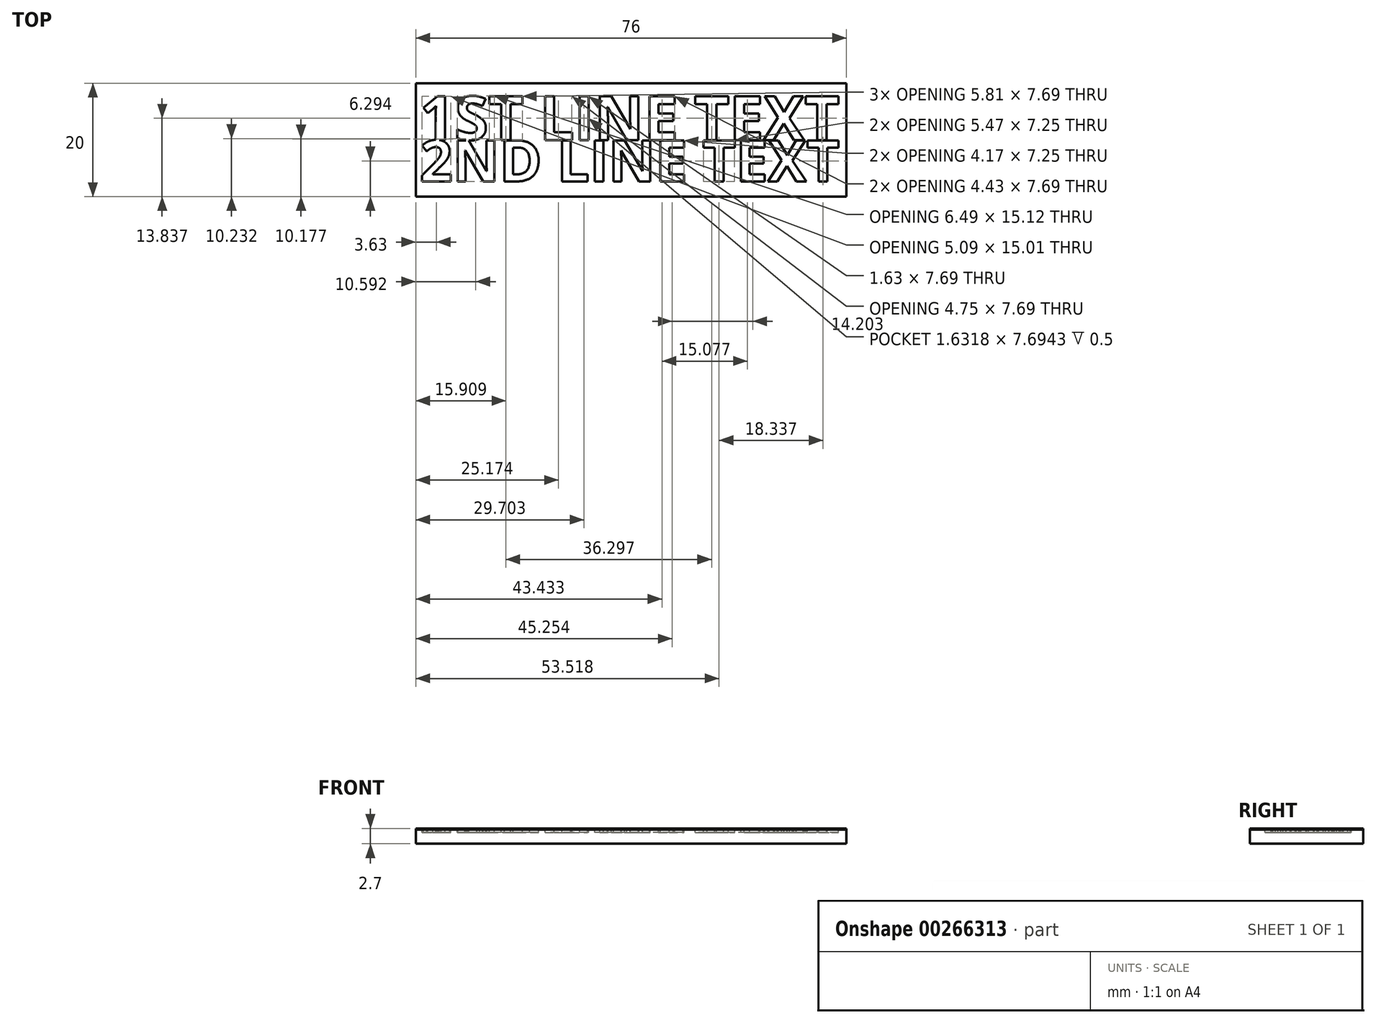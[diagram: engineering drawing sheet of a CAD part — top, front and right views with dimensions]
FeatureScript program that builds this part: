
annotation { "Feature Type Name" : "Feature", "Feature Type Description" : "" }
export const myFeature = defineFeature(function(context is Context, id is Id, definition is map)
    precondition{}
    {
        {
            var Q0;
            Q0=qCreatedBy(makeId("Top.planeOp"),FACE);
            var sketch = newSketch(context, id + "F0", { "sketchPlane" : qUnion([Q0])});
            skLineSegment(sketch, "E0.bottom", {"start": v(38, -10) * mm, "end": v(-38, -10) * mm});
            skLineSegment(sketch, "E0.top", {"start": v(38, 10) * mm, "end": v(-38, 10) * mm});
            skLineSegment(sketch, "E0.left", {"start": v(38, -10) * mm, "end": v(38, 10) * mm});
            skLineSegment(sketch, "E0.right", {"start": v(-38, -10) * mm, "end": v(-38, 10) * mm});
            skPoint(sketch, "E0.middle", {"position": v(0, 0) * mm});
            skSolve(sketch);
        }
        {
            var Q0;
            Q0=makeQuery(id+"F0.imprint","IMPRINT",FACE,{"disambiguationData":[TD([[makeQuery(id+"F0.imprint","IMPRINT",EDGE,{"derivedFrom":sQuery(id+"F0.wireOp",EDGE,"E0.bottom")}),-1.0]])]});
            extrude(context, id + "F1", {"entities" : qUnion([Q0]), "depth" : 2.5 * mm});
        }
        {
            var Q0;
            Q0=makeQuery(id+"F1.opExtrude","CAP_FACE",FACE,{"disambiguationData":[OSD([sQuery(id+"F0.wireOp",EDGE,"E0.bottom"),sQuery(id+"F0.wireOp",EDGE,"E0.top"),sQuery(id+"F0.wireOp",EDGE,"E0.left"),sQuery(id+"F0.wireOp",EDGE,"E0.right")])],"isStart":false});
            var sketch = newSketch(context, id + "F2", { "sketchPlane" : qUnion([Q0])});
            skText(sketch, "E1", { "text": "1ST LINE TEXT", "fontName": "OpenSans-Bold.ttf"});
            skText(sketch, "E2", { "text": "2ND LINE TEXT", "fontName": "OpenSans-Bold.ttf"});
            const initialGuessF2  = {"E1": [-0.0373, -1e-05, 1, 0, 0.00776], "E2": [-0.0373, -0.00733, 1, 0, 0.00731]};
            skSetInitialGuess(sketch, initialGuessF2);
            skSolve(sketch);
        }
        {
            var Q0;
            Q0=qSketchRegion(id+"F2",true);
            extrude(context, id + "F3", {"entities" : qUnion([Q0]), "operationType" : NewBodyOperationType.REMOVE, "oppositeDirection" : true, "depth" : 0.5 * mm});
        }
        {
            var Q0;
            {var subQ0=sQuery(id+"F0.wireOp",EDGE,"E0.bottom");var subQ1=sQuery(id+"F0.wireOp",EDGE,"E0.right");var subQ2=sQuery(id+"F0.wireOp",EDGE,"E0.left");var subQ3=sQuery(id+"F0.wireOp",EDGE,"E0.top");Q0=makeQuery(id+"F3.boolean.opBoolean","SPLIT",FACE,{"disambiguationData":[TD([makeQuery(id+"F1.opExtrude","SWEPT_FACE",FACE,{"disambiguationData":[OSD([subQ0])]})])],"derivedFrom":makeQuery(id+"F1.opExtrude","CAP_FACE",FACE,{"disambiguationData":[OSD([subQ0,subQ3,subQ2,subQ1])],"isStart":false})});}
            var Q1;
            Q1=makeQuery(id+"F3.boolean.opBoolean","SPLIT",FACE,{"disambiguationData":[TD([makeQuery(id+"F3.opExtrude","SWEPT_FACE",FACE,{"disambiguationData":[OSD([sQuery(id+"F2.wireOp",EDGE,"E1.sketch_text.stroke-8")])]})])],"derivedFrom":makeQuery(id+"F1.opExtrude","CAP_FACE",FACE,{"disambiguationData":[OSD([sQuery(id+"F0.wireOp",EDGE,"E0.bottom"),sQuery(id+"F0.wireOp",EDGE,"E0.top"),sQuery(id+"F0.wireOp",EDGE,"E0.left"),sQuery(id+"F0.wireOp",EDGE,"E0.right")])],"isStart":false})});
            var Q2;
            Q2=makeQuery(id+"F3.boolean.opBoolean","SPLIT",FACE,{"disambiguationData":[TD([makeQuery(id+"F3.opExtrude","SWEPT_FACE",FACE,{"disambiguationData":[OSD([sQuery(id+"F2.wireOp",EDGE,"E2.sketch_text.stroke-45")])]})])],"derivedFrom":makeQuery(id+"F1.opExtrude","CAP_FACE",FACE,{"disambiguationData":[OSD([sQuery(id+"F0.wireOp",EDGE,"E0.bottom"),sQuery(id+"F0.wireOp",EDGE,"E0.top"),sQuery(id+"F0.wireOp",EDGE,"E0.left"),sQuery(id+"F0.wireOp",EDGE,"E0.right")])],"isStart":false})});
            extrude(context, id + "F4", {"entities" : qUnion([Q0, Q1, Q2]), "depth" : 0.2 * mm});
        }
    });
